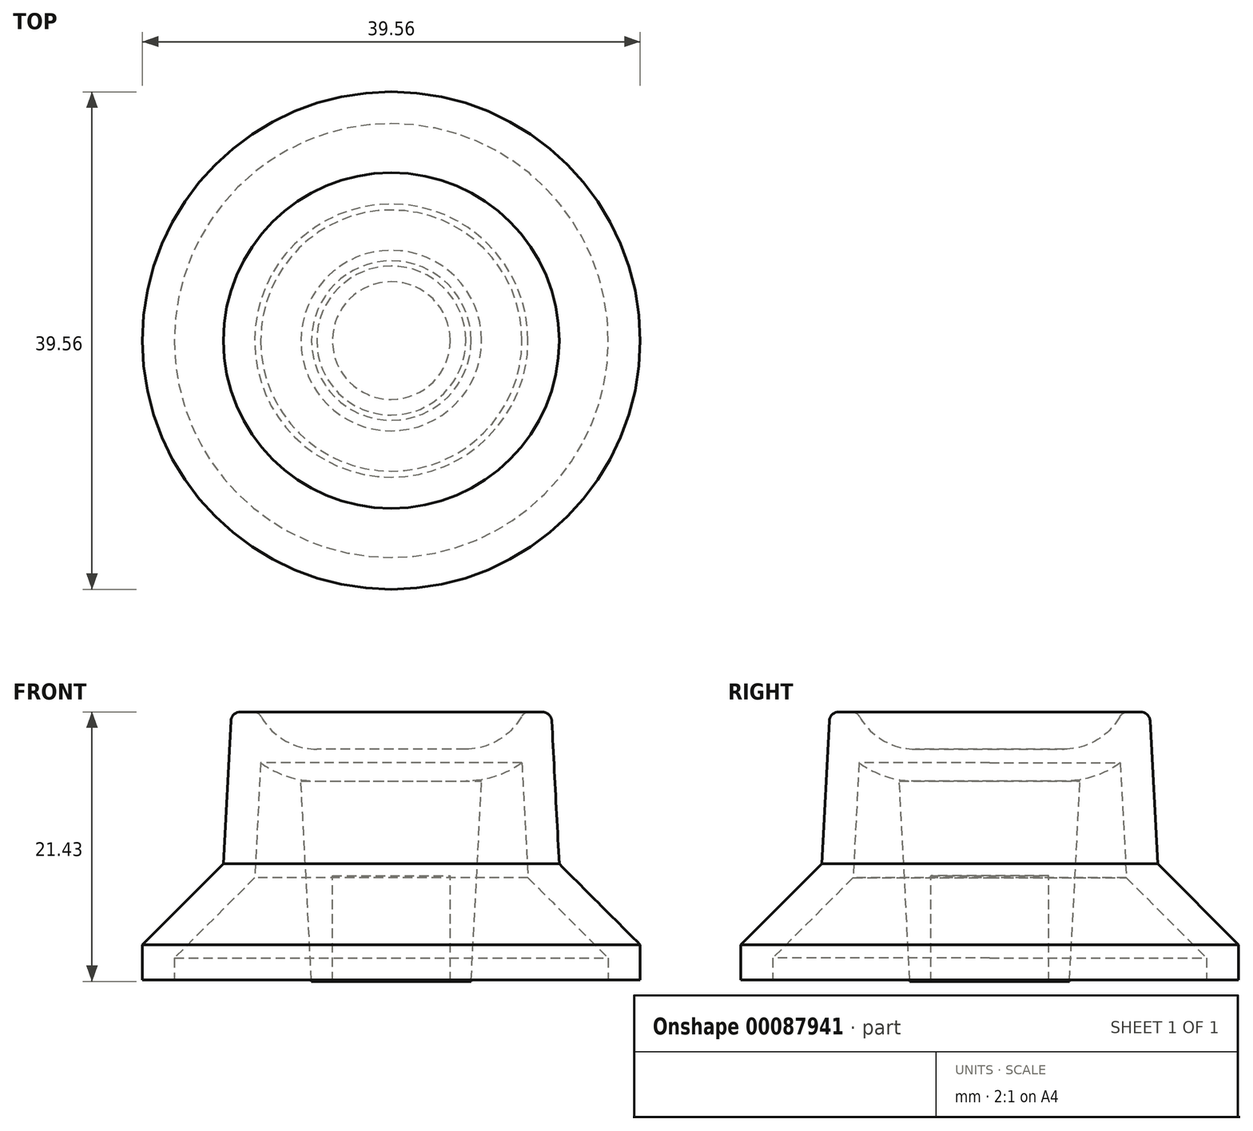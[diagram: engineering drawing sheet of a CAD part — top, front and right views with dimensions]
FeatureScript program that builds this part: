
annotation { "Feature Type Name" : "Feature", "Feature Type Description" : "" }
export const myFeature = defineFeature(function(context is Context, id is Id, definition is map)
    precondition{}
    {
        {
            var Q0;
            Q0=qCreatedBy(makeId("Top.planeOp"),FACE);
            var sketch = newSketch(context, id + "F0", { "sketchPlane" : qUnion([Q0])});
            skCircle(sketch, "E0", {"center": v(0, 0) * mm, "radius": 19.78 * mm});
            skSolve(sketch);
        }
        {
            var Q0;
            Q0=makeQuery(id+"F0.imprint","IMPRINT",FACE,{"disambiguationData":[TD([[makeQuery(id+"F0.imprint","IMPRINT",EDGE,{"derivedFrom":sQuery(id+"F0.wireOp",EDGE,"E0")}),1.0]])]});
            extrude(context, id + "F1", {"entities" : qUnion([Q0]), "depth" : 2.8 * mm});
        }
        {
            var Q0;
            Q0=makeQuery(id+"F1.opExtrude","CAP_FACE",FACE,{"disambiguationData":[OSD([sQuery(id+"F0.wireOp",EDGE,"E0")])],"isStart":false});
            extrude(context, id + "F2", {"entities" : qUnion([Q0]), "operationType" : NewBodyOperationType.ADD, "depth" : 6.44 * mm, "hasDraft" : true, "draftAngle" : 45 * degree, "draftPullDirection" : true});
        }
        {
            var Q0;
            Q0=makeQuery(id+"F2.opExtrude","CAP_FACE",FACE,{"disambiguationData":[OSD([sQuery(id+"F0.wireOp",EDGE,"E0")])],"isStart":false});
            extrude(context, id + "F3", {"entities" : qUnion([Q0]), "operationType" : NewBodyOperationType.ADD, "depth" : 12.1 * mm, "hasDraft" : true, "draftAngle" : 3 * degree, "draftPullDirection" : true});
        }
        {
            var Q0;
            Q0=makeQuery(id+"F3.opExtrude","CAP_FACE",FACE,{"disambiguationData":[OSD([sQuery(id+"F0.wireOp",EDGE,"E0")])],"isStart":false});
            var sketch = newSketch(context, id + "F4", { "sketchPlane" : qUnion([Q0])});
            skCircle(sketch, "E1", {"center": v(0, 0) * mm, "radius": 10.24 * mm});
            skSolve(sketch);
        }
        {
            var Q0;
            Q0 = qSketchRegion(id + "F4", true);
            extrude(context, id + "F5", {"entities" : qUnion([Q0]), "operationType" : NewBodyOperationType.REMOVE, "endBound" : BoundingType.SYMMETRIC, "depth" : 5.9 * mm});
        }
        {
            var Q0;
            Q0=makeQuery(id+"F3.opExtrude","CAP_EDGE",EDGE,{"disambiguationData":[OSD([sQuery(id+"F0.wireOp",EDGE,"E0")])],"isStart":false});
            var Q1;
            Q1=makeQuery(id+"F5.boolean.opBoolean","INTERSECT",EDGE,{"derivedFrom":[makeQuery(id+"F3.opExtrude","CAP_FACE",FACE,{"disambiguationData":[OSD([sQuery(id+"F0.wireOp",EDGE,"E0")])],"isStart":false}),makeQuery(id+"F5.opExtrude","SWEPT_FACE",FACE,{"disambiguationData":[OSD([sQuery(id+"F4.wireOp",EDGE,"E1")])]})]});
            fillet(context, id + "F6", {"entities" : qUnion([Q0, Q1]), "radius" : 0.76 * mm, "tangentPropagation" : true, "allowEdgeOverflow" : false});
        }
        {
            var Q0;
            Q0=makeQuery(id+"F5.boolean.opBoolean","COPY",EDGE,{"derivedFrom":makeQuery(id+"F5.opExtrude","CAP_EDGE",EDGE,{"disambiguationData":[OSD([sQuery(id+"F4.wireOp",EDGE,"E1")])],"isStart":true})});
            fillet(context, id + "F7", {"entities" : qUnion([Q0]), "radius" : 5.08 * mm, "tangentPropagation" : true, "allowEdgeOverflow" : false});
        }
        {
            var Q0;
            Q0=makeQuery(id+"F1.opExtrude","CAP_FACE",FACE,{"disambiguationData":[OSD([sQuery(id+"F0.wireOp",EDGE,"E0")])],"isStart":true});
            shell(context, id + "F8", {"entities" : qUnion([Q0]), "thickness" : 2.54 * mm});
        }
        {
            var Q0;
            {var subQ0=sQuery(id+"F4.wireOp",EDGE,"E1");Q0=makeQuery(id+"F8.opShell","OFFSET_FACE",FACE,{"disambiguationData":[OSD([subQ0]),TDD([makeQuery(id+"F5.boolean.opBoolean","COPY",FACE,{"derivedFrom":makeQuery(id+"F5.opExtrude","CAP_FACE",FACE,{"disambiguationData":[OSD([subQ0])],"isStart":true})})])]});}
            var sketch = newSketch(context, id + "F9", { "sketchPlane" : qUnion([Q0])});
            skCircle(sketch, "E2", {"center": v(0, 0) * mm, "radius": 7.18 * mm});
            skSolve(sketch);
        }
        {
            var Q0;
            Q0 = qSketchRegion(id + "F9", true);
            extrude(context, id + "F10", {"entities" : qUnion([Q0]), "operationType" : NewBodyOperationType.ADD, "depth" : 15.93 * mm, "hasDraft" : true, "draftAngle" : 3 * degree, "draftPullDirection" : true});
        }
        {
            var Q0;
            Q0=makeQuery(id+"F10.opExtrude","CAP_FACE",FACE,{"disambiguationData":[OSD([sQuery(id+"F9.wireOp",EDGE,"E2")])],"isStart":false});
            var sketch = newSketch(context, id + "F11", { "sketchPlane" : qUnion([Q0])});
            skCircle(sketch, "E3", {"center": v(0, 0) * mm, "radius": 4.68 * mm});
            skSolve(sketch);
        }
        {
            var Q0;
            Q0 = qSketchRegion(id + "F11", true);
            extrude(context, id + "F12", {"entities" : qUnion([Q0]), "operationType" : NewBodyOperationType.REMOVE, "endBound" : BoundingType.SYMMETRIC, "depth" : 16.8 * mm});
        }
    });
